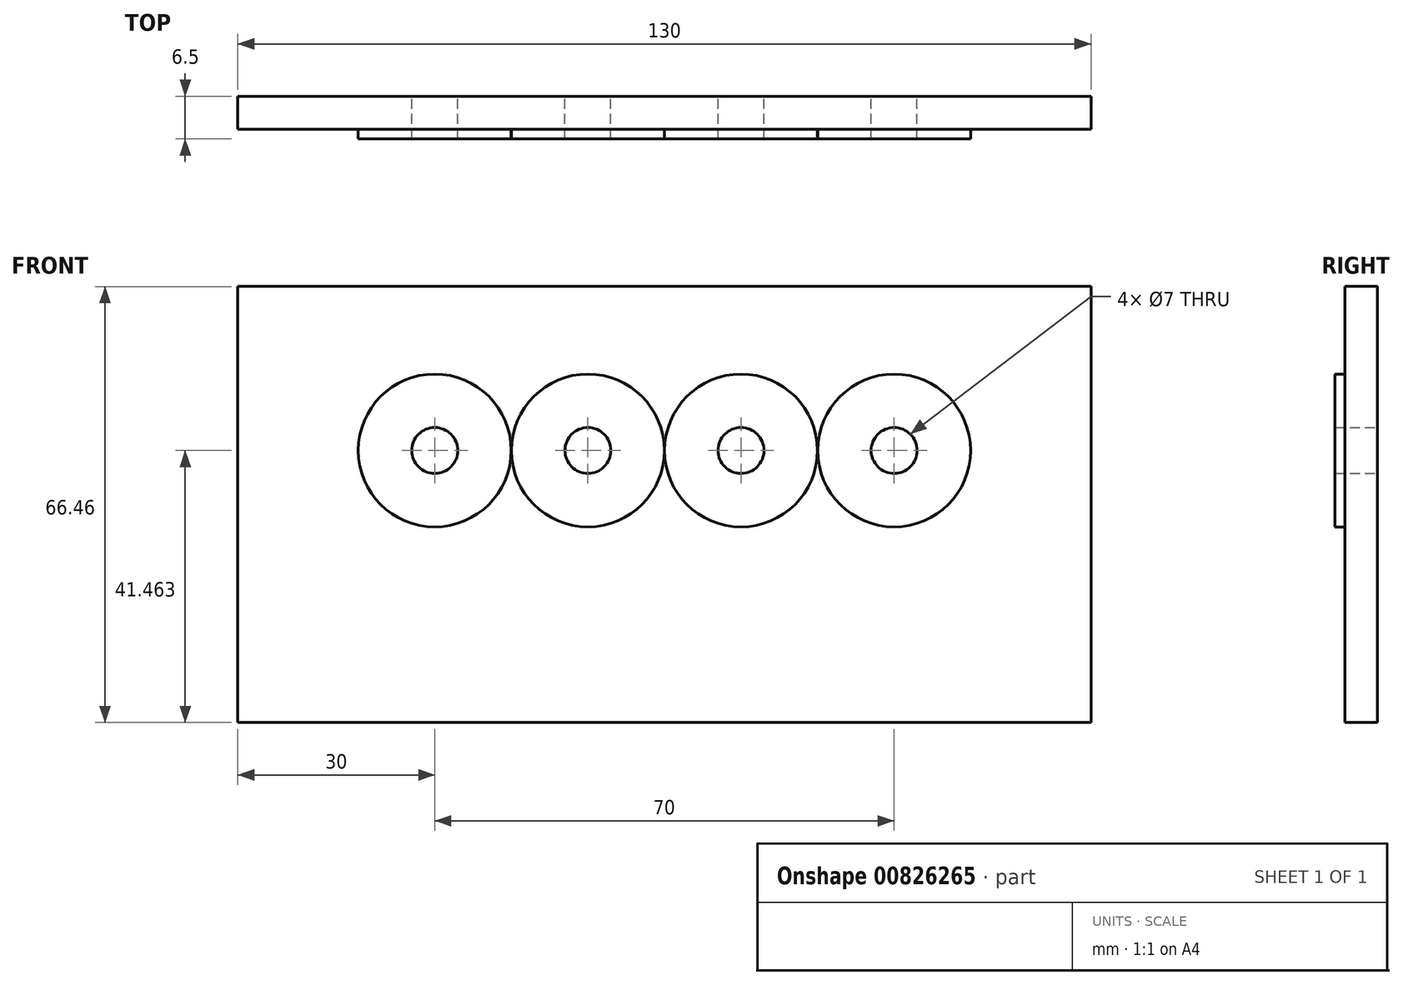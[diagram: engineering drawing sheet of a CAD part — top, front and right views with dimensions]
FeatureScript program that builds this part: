
annotation { "Feature Type Name" : "Feature", "Feature Type Description" : "" }
export const myFeature = defineFeature(function(context is Context, id is Id, definition is map)
    precondition{}
    {
        {
            var Q0;
            Q0=qCreatedBy(makeId("Front.planeOp"),FACE);
            var sketch = newSketch(context, id + "F0", { "sketchPlane" : qUnion([Q0])});
            skLineSegment(sketch, "E0", {"start": v(-65, 33.23) * mm, "end": v(65, 33.23) * mm});
            skLineSegment(sketch, "E1", {"start": v(65, 33.23) * mm, "end": v(65, -33.23) * mm});
            skLineSegment(sketch, "E2", {"start": v(65, -33.23) * mm, "end": v(-65, -33.23) * mm});
            skLineSegment(sketch, "E3", {"start": v(-65, -33.23) * mm, "end": v(-65, 33.23) * mm});
            skLineSegment(sketch, "E4", {"start": v(0, 0) * mm, "end": v(0, 33.23) * mm, "construction": true});
            skLineSegment(sketch, "E5", {"start": v(0, 0) * mm, "end": v(-65, 0) * mm, "construction": true});
            skCircle(sketch, "E6", {"center": v(35, 8.23) * mm, "radius": 11.65 * mm});
            skCircle(sketch, "E7", {"center": v(-35, 8.23) * mm, "radius": 11.65 * mm});
            skLineSegment(sketch, "E8", {"start": v(-35, 8.23) * mm, "end": v(-35, 33.23) * mm, "construction": true});
            skLineSegment(sketch, "E9", {"start": v(-35, 8.23) * mm, "end": v(-65, 8.23) * mm, "construction": true});
            skLineSegment(sketch, "E10", {"start": v(65, 8.23) * mm, "end": v(35, 8.23) * mm, "construction": true});
            skLineSegment(sketch, "E11", {"start": v(35, 8.23) * mm, "end": v(35, 33.23) * mm, "construction": true});
            skLineSegment(sketch, "E12", {"start": v(-35, 8.23) * mm, "end": v(0, 8.23) * mm, "construction": true});
            skLineSegment(sketch, "E13", {"start": v(35, 8.23) * mm, "end": v(0, 8.23) * mm, "construction": true});
            skCircle(sketch, "E14", {"center": v(-35, 8.23) * mm, "radius": 3.5 * mm});
            skCircle(sketch, "E15", {"center": v(35, 8.23) * mm, "radius": 3.5 * mm});
            skLineSegment(sketch, "E16", {"start": v(-23.33, 8.23) * mm, "end": v(-23.33, 33.23) * mm, "construction": true});
            skLineSegment(sketch, "E17", {"start": v(-11.67, 8.23) * mm, "end": v(-11.67, 33.23) * mm, "construction": true});
            skLineSegment(sketch, "E18", {"start": v(0, 8.23) * mm, "end": v(0, 33.23) * mm});
            skLineSegment(sketch, "E19", {"start": v(11.67, 8.23) * mm, "end": v(11.67, 33.23) * mm, "construction": true});
            skLineSegment(sketch, "E20", {"start": v(23.33, 33.23) * mm, "end": v(23.33, 8.23) * mm, "construction": true});
            skCircle(sketch, "E21", {"center": v(-11.67, 8.23) * mm, "radius": 11.65 * mm});
            skCircle(sketch, "E22", {"center": v(11.67, 8.23) * mm, "radius": 11.65 * mm});
            skCircle(sketch, "E23", {"center": v(-11.67, 8.23) * mm, "radius": 3.5 * mm});
            skCircle(sketch, "E24", {"center": v(11.67, 8.23) * mm, "radius": 3.5 * mm});
            skSolve(sketch);
        }
        {
            var Q0;
            Q0=makeQuery(id+"F0.imprint","IMPRINT",FACE,{"disambiguationData":[TD([[makeQuery(id+"F0.imprint","IMPRINT",EDGE,{"derivedFrom":sQuery(id+"F0.wireOp",EDGE,"E21")}),1.0]])]});
            var Q1;
            Q1=makeQuery(id+"F0.imprint","IMPRINT",FACE,{"disambiguationData":[TD([[makeQuery(id+"F0.imprint","IMPRINT",EDGE,{"derivedFrom":sQuery(id+"F0.wireOp",EDGE,"E22")}),1.0]])]});
            var Q2;
            Q2=makeQuery(id+"F0.imprint","IMPRINT",FACE,{"disambiguationData":[TD([[makeQuery(id+"F0.imprint","IMPRINT",EDGE,{"derivedFrom":sQuery(id+"F0.wireOp",EDGE,"E6")}),1.0]])]});
            var Q3;
            Q3=makeQuery(id+"F0.imprint","IMPRINT",FACE,{"disambiguationData":[TD([[makeQuery(id+"F0.imprint","IMPRINT",EDGE,{"derivedFrom":sQuery(id+"F0.wireOp",EDGE,"E7")}),1.0]])]});
            var Q4;
            {var subQ0=sQuery(id+"F0.wireOp",EDGE,"E1");Q4=makeQuery(id+"F0.imprint","IMPRINT",FACE,{"disambiguationData":[TD([[makeQuery(id+"F0.imprint","IMPRINT",EDGE,{"derivedFrom":subQ0}),-1.0]])]});}
            extrude(context, id + "F1", {"entities" : qUnion([Q0, Q1, Q2, Q3, Q4]), "endBound" : BoundingType.SYMMETRIC, "depth" : 5 * mm, "offsetDistance" : 25 * mm});
        }
        {
            var Q0;
            Q0=makeQuery(id+"F0.imprint","IMPRINT",FACE,{"disambiguationData":[TD([[makeQuery(id+"F0.imprint","IMPRINT",EDGE,{"derivedFrom":sQuery(id+"F0.wireOp",EDGE,"E6")}),1.0]])]});
            extrude(context, id + "F2", {"entities" : qUnion([Q0]), "operationType" : NewBodyOperationType.ADD, "depth" : 4 * mm, "offsetDistance" : 25 * mm});
        }
        {
            var Q0;
            Q0=makeQuery(id+"F0.imprint","IMPRINT",FACE,{"disambiguationData":[TD([[makeQuery(id+"F0.imprint","IMPRINT",EDGE,{"derivedFrom":sQuery(id+"F0.wireOp",EDGE,"E7")}),1.0]])]});
            extrude(context, id + "F3", {"entities" : qUnion([Q0]), "operationType" : NewBodyOperationType.ADD, "depth" : 4 * mm, "offsetDistance" : 25 * mm});
        }
        {
            var Q0;
            Q0=makeQuery(id+"F0.imprint","IMPRINT",FACE,{"disambiguationData":[TD([[makeQuery(id+"F0.imprint","IMPRINT",EDGE,{"derivedFrom":sQuery(id+"F0.wireOp",EDGE,"E21")}),1.0]])]});
            extrude(context, id + "F4", {"entities" : qUnion([Q0]), "operationType" : NewBodyOperationType.ADD, "depth" : 4 * mm, "offsetDistance" : 25 * mm});
        }
        {
            var Q0;
            Q0=makeQuery(id+"F0.imprint","IMPRINT",FACE,{"disambiguationData":[TD([[makeQuery(id+"F0.imprint","IMPRINT",EDGE,{"derivedFrom":sQuery(id+"F0.wireOp",EDGE,"E22")}),1.0]])]});
            extrude(context, id + "F5", {"entities" : qUnion([Q0]), "operationType" : NewBodyOperationType.ADD, "depth" : 4 * mm, "offsetDistance" : 25 * mm});
        }
        {
            var Q0;
            Q0=makeQuery(id+"F0.imprint","IMPRINT",FACE,{"disambiguationData":[TD([[makeQuery(id+"F0.imprint","IMPRINT",EDGE,{"derivedFrom":sQuery(id+"F0.wireOp",EDGE,"E22")}),1.0]])]});
            extrude(context, id + "F6", {"entities" : qUnion([Q0]), "operationType" : NewBodyOperationType.ADD, "depth" : 4 * mm, "offsetDistance" : 25 * mm});
        }
    });
